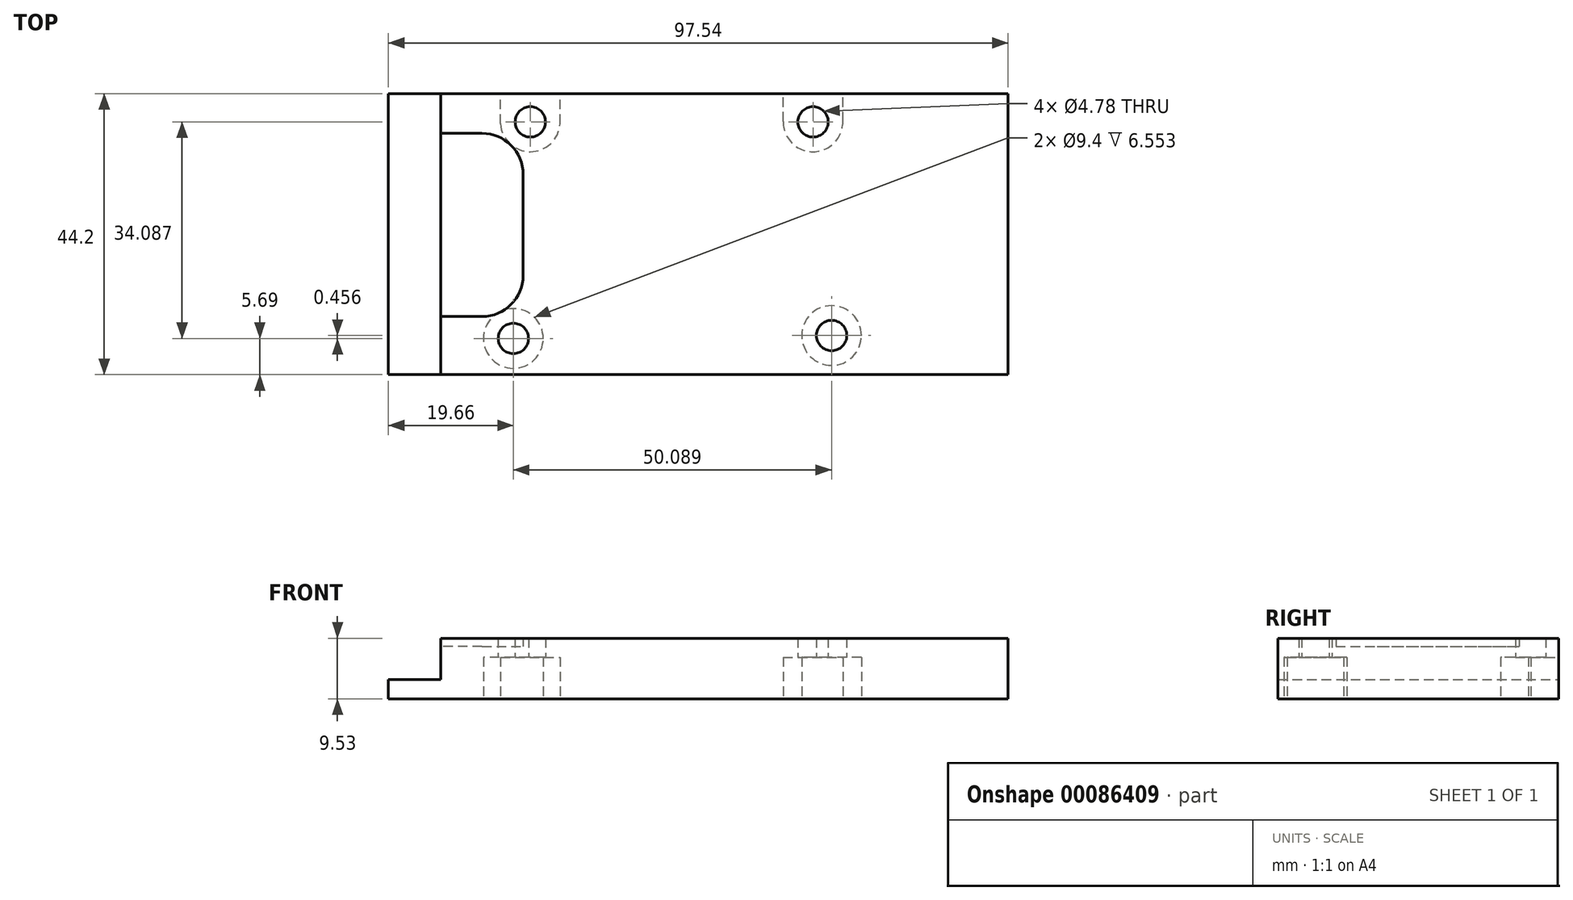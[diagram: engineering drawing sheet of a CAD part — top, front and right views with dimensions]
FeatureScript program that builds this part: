
annotation { "Feature Type Name" : "Feature", "Feature Type Description" : "" }
export const myFeature = defineFeature(function(context is Context, id is Id, definition is map)
    precondition{}
    {
        {
            var Q0;
            Q0=qCreatedBy(makeId("Top.planeOp"),FACE);
            var sketch = newSketch(context, id + "F0", { "sketchPlane" : qUnion([Q0])});
            skLineSegment(sketch, "E0.bottom", {"start": v(0, 0) * mm, "end": v(97.54, 0) * mm});
            skLineSegment(sketch, "E0.top", {"start": v(0, 44.2) * mm, "end": v(97.54, 44.2) * mm});
            skLineSegment(sketch, "E0.left", {"start": v(0, 0) * mm, "end": v(0, 44.2) * mm});
            skLineSegment(sketch, "E0.right", {"start": v(97.54, 0) * mm, "end": v(97.54, 44.2) * mm});
            skLineSegment(sketch, "E1", {"start": v(8.26, 0) * mm, "end": v(8.25, 44.2) * mm});
            skLineSegment(sketch, "E2", {"start": v(21.2, 0) * mm, "end": v(21.2, 44.2) * mm, "construction": true});
            skLineSegment(sketch, "E3", {"start": v(8.26, 9.14) * mm, "end": v(21.2, 9.14) * mm, "construction": true});
            skLineSegment(sketch, "E4", {"start": v(8.25, 37.97) * mm, "end": v(21.2, 37.97) * mm, "construction": true});
            skCircle(sketch, "E5", {"center": v(14.73, 15.62) * mm, "radius": 6.48 * mm, "construction": true});
            skCircle(sketch, "E6", {"center": v(14.73, 31.5) * mm, "radius": 6.48 * mm, "construction": true});
            skArc(sketch, "E7", {"start": v(21.2, 31.5) * mm, "mid": v(19.31, 36.08) * mm, "end": v(14.73, 37.97) * mm});
            skArc(sketch, "E8", {"start": v(14.73, 9.14) * mm, "mid": v(19.31, 11.04) * mm, "end": v(21.2, 15.62) * mm});
            skLineSegment(sketch, "E9", {"start": v(21.2, 15.62) * mm, "end": v(21.2, 31.5) * mm});
            skLineSegment(sketch, "E10", {"start": v(14.73, 37.97) * mm, "end": v(8.25, 37.97) * mm});
            skLineSegment(sketch, "E11", {"start": v(14.73, 9.14) * mm, "end": v(8.26, 9.14) * mm});
            skCircle(sketch, "E12", {"center": v(22.33, 39.78) * mm, "radius": 2.39 * mm});
            skCircle(sketch, "E13", {"center": v(19.66, 5.69) * mm, "radius": 2.39 * mm});
            skCircle(sketch, "E14", {"center": v(66.83, 39.78) * mm, "radius": 2.39 * mm});
            skCircle(sketch, "E15", {"center": v(69.75, 6.15) * mm, "radius": 2.39 * mm});
            skSolve(sketch);
        }
        {
            var Q0;
            {var subQ4=sQuery(id+"F0.wireOp",EDGE,"E0.left");Q0=makeQuery(id+"F0.imprint","IMPRINT",FACE,{"disambiguationData":[TD([[makeQuery(id+"F0.imprint","IMPRINT",EDGE,{"derivedFrom":subQ4}),-1.0]])]});}
            extrude(context, id + "F1", {"entities" : qUnion([Q0]), "depth" : 3.05 * mm});
        }
        {
            var Q0;
            Q0=makeQuery(id+"F0.imprint","IMPRINT",FACE,{"disambiguationData":[TD([[makeQuery(id+"F0.imprint","IMPRINT",EDGE,{"derivedFrom":sQuery(id+"F0.wireOp",EDGE,"E7")}),1.0]])]});
            extrude(context, id + "F2", {"entities" : qUnion([Q0]), "operationType" : NewBodyOperationType.ADD, "depth" : 8.23 * mm});
        }
        {
            var Q0;
            {var subQ4=sQuery(id+"F0.wireOp",EDGE,"E0.right");Q0=makeQuery(id+"F0.imprint","IMPRINT",FACE,{"disambiguationData":[TD([[makeQuery(id+"F0.imprint","IMPRINT",EDGE,{"derivedFrom":subQ4}),1.0]])]});}
            extrude(context, id + "F3", {"entities" : qUnion([Q0]), "operationType" : NewBodyOperationType.ADD, "depth" : 9.52 * mm});
        }
        {
            var Q0;
            {var subQ4=sQuery(id+"F0.wireOp",EDGE,"E0.right");Q0=makeQuery(id+"F0.imprint","IMPRINT",FACE,{"disambiguationData":[TD([[makeQuery(id+"F0.imprint","IMPRINT",EDGE,{"derivedFrom":subQ4}),1.0]])]});}
            var sketch = newSketch(context, id + "F4", { "sketchPlane" : qUnion([Q0])});
            skCircle(sketch, "E16", {"center": v(69.75, 6.15) * mm, "radius": 4.7 * mm});
            skCircle(sketch, "E17", {"center": v(66.83, 39.78) * mm, "radius": 4.7 * mm, "construction": true});
            skCircle(sketch, "E18", {"center": v(22.33, 39.78) * mm, "radius": 4.7 * mm, "construction": true});
            skCircle(sketch, "E19", {"center": v(19.66, 5.69) * mm, "radius": 4.7 * mm});
            skLineSegment(sketch, "E20", {"start": v(71.53, 39.84) * mm, "end": v(71.53, 44.2) * mm});
            skLineSegment(sketch, "E21", {"start": v(62.13, 39.84) * mm, "end": v(62.13, 44.2) * mm});
            skArc(sketch, "E22", {"start": v(62.13, 39.84) * mm, "mid": v(67.17, 35.09) * mm, "end": v(71.47, 40.51) * mm});
            skLineSegment(sketch, "E23", {"start": v(66.83, 39.78) * mm, "end": v(66.83, 44.13) * mm, "construction": true});
            skLineSegment(sketch, "E24", {"start": v(22.33, 39.78) * mm, "end": v(22.33, 44.5) * mm, "construction": true});
            skLineSegment(sketch, "E25", {"start": v(27.02, 39.48) * mm, "end": v(27.02, 44.2) * mm});
            skLineSegment(sketch, "E26", {"start": v(17.64, 39.48) * mm, "end": v(17.64, 44.2) * mm});
            skArc(sketch, "E27", {"start": v(17.64, 39.48) * mm, "mid": v(22.33, 35.08) * mm, "end": v(27.02, 39.48) * mm});
            skSolve(sketch);
        }
        {
            var Q0;
            Q0 = qSketchRegion(id + "F4", true);
            var Q1;
            {var subQ2=sQuery(id+"F4.wireOp",EDGE,"E20");Q1=makeQuery(id+"F4.imprint","IMPRINT",FACE,{"disambiguationData":[TD([[makeQuery(id+"F4.imprint","IMPRINT",EDGE,{"derivedFrom":subQ2}),1.0]])]});}
            var Q2;
            {var subQ0=sQuery(id+"F4.wireOp",EDGE,"E25");Q2=makeQuery(id+"F4.imprint","IMPRINT",FACE,{"disambiguationData":[TD([[makeQuery(id+"F4.imprint","IMPRINT",EDGE,{"derivedFrom":subQ0}),1.0]])]});}
            extrude(context, id + "F5", {"entities" : qUnion([Q0, Q1, Q2]), "operationType" : NewBodyOperationType.REMOVE, "depth" : 6.55 * mm});
        }
    });
